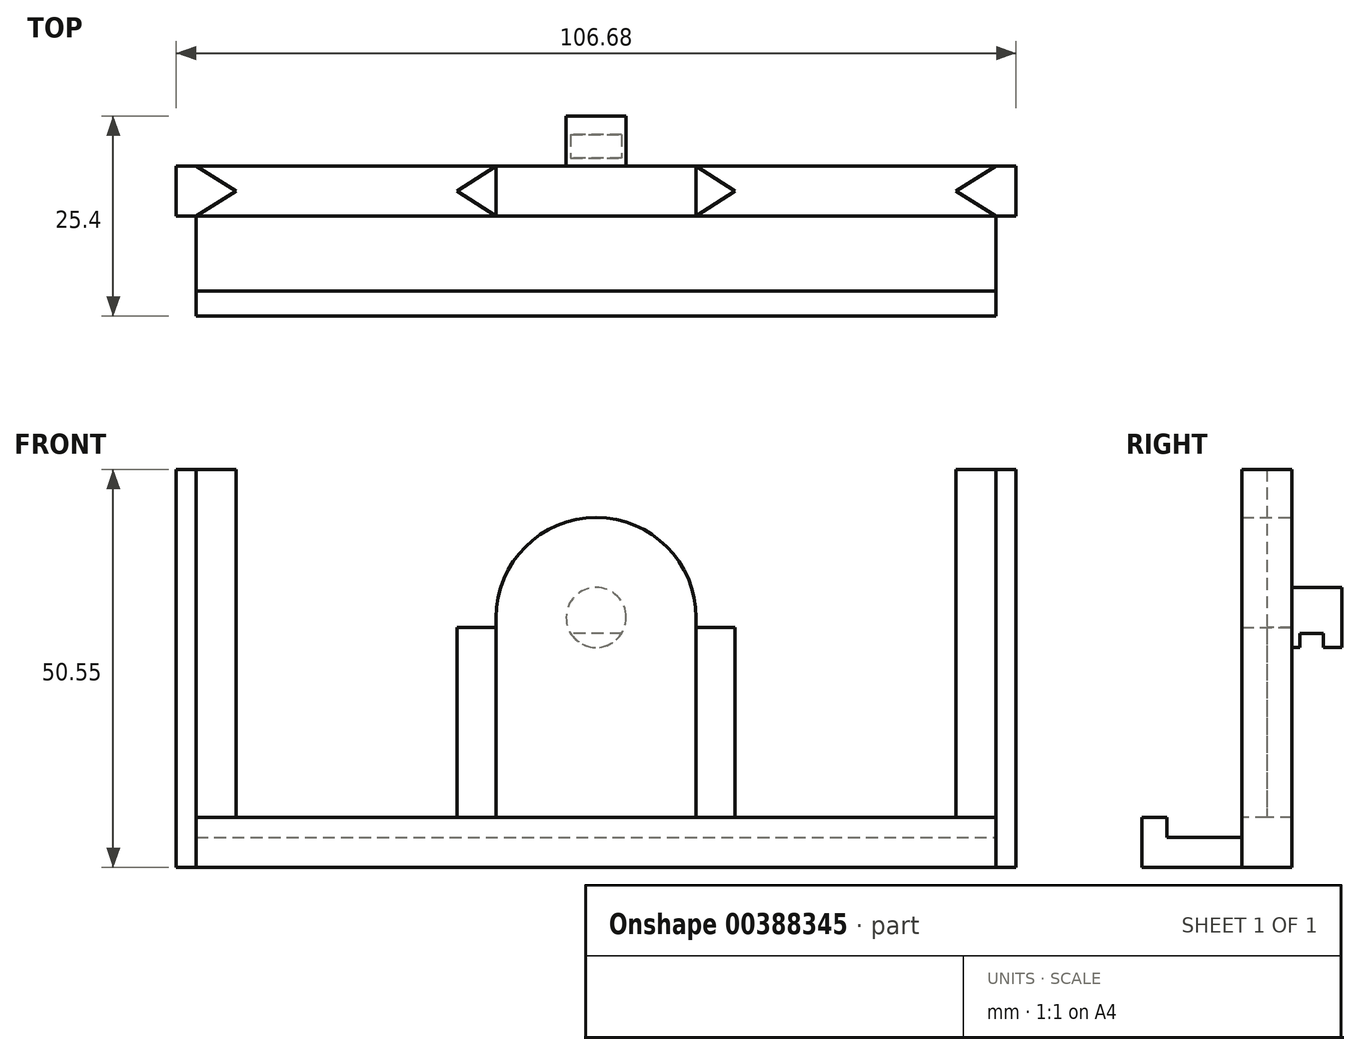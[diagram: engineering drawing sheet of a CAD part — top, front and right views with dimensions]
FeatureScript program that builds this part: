
annotation { "Feature Type Name" : "Feature", "Feature Type Description" : "" }
export const myFeature = defineFeature(function(context is Context, id is Id, definition is map)
    precondition{}
    {
        {
            var Q0;
            Q0=qCreatedBy(makeId("Front.planeOp"),FACE);
            var sketch = newSketch(context, id + "F0", { "sketchPlane" : qUnion([Q0])});
            skLineSegment(sketch, "E0.bottom", {"start": v(0, 0) * mm, "end": v(25.4, 0) * mm});
            skLineSegment(sketch, "E0.left", {"start": v(0, 0) * mm, "end": v(0, 25.4) * mm});
            skLineSegment(sketch, "E0.right", {"start": v(25.4, 0) * mm, "end": v(25.4, 25.4) * mm});
            skArc(sketch, "E1", {"start": v(25.4, 25.4) * mm, "mid": v(12.7, 38.1) * mm, "end": v(0, 25.4) * mm});
            skSolve(sketch);
        }
        {
            var Q0;
            Q0=qSketchRegion(id+"F0",true);
            extrude(context, id + "F1", {"entities" : qUnion([Q0]), "depth" : 6.35 * mm});
        }
        {
            var Q0;
            Q0=makeQuery(id+"F1.opExtrude","SWEPT_FACE",FACE,{"disambiguationData":[OSD([sQuery(id+"F0.wireOp",EDGE,"E0.bottom")])]});
            var sketch = newSketch(context, id + "F2", { "sketchPlane" : qUnion([Q0])});
            skPoint(sketch, "E2.endSnap0", {"position": v(25.4, 3.18) * mm});
            skLineSegment(sketch, "E3", {"start": v(0, 0) * mm, "end": v(-4.95, 3.18) * mm});
            skLineSegment(sketch, "E4", {"start": v(0, 6.35) * mm, "end": v(-4.95, 3.18) * mm});
            skLineSegment(sketch, "E5", {"start": v(25.4, 6.35) * mm, "end": v(30.35, 3.18) * mm});
            skLineSegment(sketch, "E6", {"start": v(30.35, 3.18) * mm, "end": v(30.35, 3.18) * mm});
            skLineSegment(sketch, "E7", {"start": v(25.4, 0) * mm, "end": v(30.35, 3.18) * mm});
            skPoint(sketch, "E8.start.orphan", {"position": v(0, 3.18) * mm});
            skPoint(sketch, "E2.start.orphan", {"position": v(25.4, 3.18) * mm});
            skLineSegment(sketch, "E9", {"start": v(0, 0) * mm, "end": v(0, 6.35) * mm});
            skLineSegment(sketch, "E10", {"start": v(25.4, 6.35) * mm, "end": v(25.4, 0) * mm});
            skSolve(sketch);
        }
        {
            var Q0;
            Q0=qSketchRegion(id+"F2",true);
            extrude(context, id + "F3", {"entities" : qUnion([Q0]), "operationType" : NewBodyOperationType.ADD, "oppositeDirection" : true, "depth" : 24.13 * mm});
        }
        {
            var Q0;
            Q0=makeQuery(id+"F3.boolean.opBoolean","MERGE",FACE,{"derivedFrom":[makeQuery(id+"F1.opExtrude","SWEPT_FACE",FACE,{"disambiguationData":[OSD([sQuery(id+"F0.wireOp",EDGE,"E0.bottom")])]}),makeQuery(id+"F3.opExtrude","CAP_FACE",FACE,{"disambiguationData":[OSD([sQuery(id+"F2.wireOp",EDGE,"E3"),sQuery(id+"F2.wireOp",EDGE,"E4"),sQuery(id+"F2.wireOp",EDGE,"E9")])],"isStart":true}),makeQuery(id+"F3.opExtrude","CAP_FACE",FACE,{"disambiguationData":[OSD([sQuery(id+"F2.wireOp",EDGE,"E5"),sQuery(id+"F2.wireOp",EDGE,"E7"),sQuery(id+"F2.wireOp",EDGE,"E10")])],"isStart":true})]});
            var sketch = newSketch(context, id + "F4", { "sketchPlane" : qUnion([Q0])});
            skLineSegment(sketch, "E11.bottom", {"start": v(63.5, 0) * mm, "end": v(-38.1, 0) * mm});
            skLineSegment(sketch, "E11.top", {"start": v(63.5, 6.35) * mm, "end": v(-38.1, 6.35) * mm});
            skLineSegment(sketch, "E11.left", {"start": v(63.5, 0) * mm, "end": v(63.5, 6.35) * mm});
            skLineSegment(sketch, "E11.right", {"start": v(-38.1, 0) * mm, "end": v(-38.1, 6.35) * mm});
            skSolve(sketch);
        }
        {
            var Q0;
            Q0=qSketchRegion(id+"F4",true);
            extrude(context, id + "F5", {"entities" : qUnion([Q0]), "operationType" : NewBodyOperationType.ADD, "depth" : 6.35 * mm});
        }
        {
            var Q0;
            Q0=makeQuery(id+"F5.boolean.opBoolean","MERGE",FACE,{"derivedFrom":[makeQuery(id+"F1.opExtrude","CAP_FACE",FACE,{"disambiguationData":[OSD([sQuery(id+"F0.wireOp",EDGE,"E0.bottom"),sQuery(id+"F0.wireOp",EDGE,"E0.left"),sQuery(id+"F0.wireOp",EDGE,"E0.right"),sQuery(id+"F0.wireOp",EDGE,"E1")])],"isStart":false}),makeQuery(id+"F5.opExtrude","SWEPT_FACE",FACE,{"disambiguationData":[OSD([sQuery(id+"F4.wireOp",EDGE,"E11.top")])]})]});
            var sketch = newSketch(context, id + "F6", { "sketchPlane" : qUnion([Q0])});
            skLineSegment(sketch, "E12", {"start": v(0, 0) * mm, "end": v(25.4, 0) * mm});
            skSolve(sketch);
        }
        {
            var Q0;
            Q0=qSketchRegion(id+"F6",true);
            var Q1;
            Q1=makeQuery(id+"F6.imprint","IMPRINT",FACE,{"disambiguationData":[TD([[makeQuery(id+"F6.imprint","IMPRINT",EDGE,{"derivedFrom":sQuery(id+"F6.wireOp",EDGE,"E12")}),-1.0]])]});
            extrude(context, id + "F7", {"entities" : qUnion([Q0, Q1]), "operationType" : NewBodyOperationType.ADD, "depth" : 12.7 * mm});
        }
        {
            var Q0;
            {var subQ0=sQuery(id+"F4.wireOp",EDGE,"E11.left");Q0=makeQuery(id+"F7.boolean.opBoolean","MERGE",FACE,{"derivedFrom":[makeQuery(id+"F5.opExtrude","SWEPT_FACE",FACE,{"disambiguationData":[OSD([subQ0])]}),makeQuery(id+"F7.opExtrude","SWEPT_FACE",FACE,{"disambiguationData":[OSD([sQuery(id+"F4.wireOp",EDGE,"E11.top"),subQ0])]})]});}
            var sketch = newSketch(context, id + "F8", { "sketchPlane" : qUnion([Q0])});
            skLineSegment(sketch, "E13.bottom", {"start": v(-15.87, 0) * mm, "end": v(-6.35, 0) * mm});
            skLineSegment(sketch, "E13.top", {"start": v(-15.87, -2.54) * mm, "end": v(-6.35, -2.54) * mm});
            skLineSegment(sketch, "E13.left", {"start": v(-15.87, 0) * mm, "end": v(-15.87, -2.54) * mm});
            skLineSegment(sketch, "E13.right", {"start": v(-6.35, 0) * mm, "end": v(-6.35, -2.54) * mm});
            skSolve(sketch);
        }
        {
            var Q0;
            Q0=qSketchRegion(id+"F8",true);
            extrude(context, id + "F9", {"entities" : qUnion([Q0]), "operationType" : NewBodyOperationType.REMOVE, "oppositeDirection" : true, "depth" : 114.28 * mm});
        }
        {
            var Q0;
            {var subQ0=sQuery(id+"F4.wireOp",EDGE,"E11.left");Q0=makeQuery(id+"F7.boolean.opBoolean","MERGE",FACE,{"derivedFrom":[makeQuery(id+"F5.opExtrude","SWEPT_FACE",FACE,{"disambiguationData":[OSD([subQ0])]}),makeQuery(id+"F7.opExtrude","SWEPT_FACE",FACE,{"disambiguationData":[OSD([sQuery(id+"F4.wireOp",EDGE,"E11.top"),subQ0])]})]});}
            var sketch = newSketch(context, id + "F10", { "sketchPlane" : qUnion([Q0])});
            skLineSegment(sketch, "E14", {"start": v(-6.35, 0) * mm, "end": v(-15.87, 0) * mm});
            skLineSegment(sketch, "E15", {"start": v(-6.35, 0) * mm, "end": v(-6.35, -6.35) * mm});
            skSolve(sketch);
        }
        {
            var Q0;
            {var subQ0=sQuery(id+"F10.wireOp",EDGE,"E14");Q0=makeQuery(id+"F10.imprint","IMPRINT",FACE,{"disambiguationData":[TD([[makeQuery(id+"F10.imprint","IMPRINT",EDGE,{"derivedFrom":subQ0}),1.0]])]});}
            extrude(context, id + "F11", {"entities" : qUnion([Q0]), "depth" : 12.7 * mm});
        }
        {
            var Q0;
            {var subQ0=sQuery(id+"F4.wireOp",EDGE,"E11.left");Q0=makeQuery(id+"F7.boolean.opBoolean","MERGE",FACE,{"derivedFrom":[makeQuery(id+"F5.opExtrude","SWEPT_FACE",FACE,{"disambiguationData":[OSD([subQ0])]}),makeQuery(id+"F7.opExtrude","SWEPT_FACE",FACE,{"disambiguationData":[OSD([sQuery(id+"F4.wireOp",EDGE,"E11.top"),subQ0])]})]});}
            var sketch = newSketch(context, id + "F12", { "sketchPlane" : qUnion([Q0])});
            skLineSegment(sketch, "E16", {"start": v(-6.35, -2.54) * mm, "end": v(-6.35, -6.35) * mm});
            skSolve(sketch);
        }
        {
            var Q0;
            Q0 = qSketchRegion(id + "F12", true);
            var Q1;
            {var subQ4=sQuery(id+"F12.wireOp",EDGE,"E16");Q1=makeQuery(id+"F12.imprint","IMPRINT",FACE,{"disambiguationData":[TD([[makeQuery(id+"F12.imprint","IMPRINT",EDGE,{"derivedFrom":subQ4}),-1.0]])]});}
            extrude(context, id + "F13", {"entities" : qUnion([Q0, Q1]), "depth" : 12.7 * mm});
        }
        {
            var Q0;
            {var subQ0=sQuery(id+"F4.wireOp",EDGE,"E11.right");Q0=makeQuery(id+"F7.boolean.opBoolean","MERGE",FACE,{"derivedFrom":[makeQuery(id+"F5.opExtrude","SWEPT_FACE",FACE,{"disambiguationData":[OSD([subQ0])]}),makeQuery(id+"F7.opExtrude","SWEPT_FACE",FACE,{"disambiguationData":[OSD([sQuery(id+"F4.wireOp",EDGE,"E11.top"),subQ0])]})]});}
            var sketch = newSketch(context, id + "F14", { "sketchPlane" : qUnion([Q0])});
            skLineSegment(sketch, "E17", {"start": v(6.35, 0) * mm, "end": v(15.87, 0) * mm});
            skSolve(sketch);
        }
        {
            var Q0;
            Q0=makeQuery(id+"F13.opExtrude","SWEPT_BODY",BODY,{"disambiguationData":[OSD([sQuery(id+"F4.wireOp",EDGE,"E11.top"),sQuery(id+"F4.wireOp",EDGE,"E11.left"),sQuery(id+"F8.wireOp",EDGE,"E13.top"),sQuery(id+"F8.wireOp",EDGE,"E13.left"),sQuery(id+"F12.wireOp",EDGE,"E16")])]});
            deleteBodies(context, id + "F15", {"entities" : qUnion([Q0])});
        }
        {
            var Q0;
            Q0=makeQuery(id+"F11.opExtrude","SWEPT_BODY",BODY,{"disambiguationData":[OSD([sQuery(id+"F8.wireOp",EDGE,"E13.top"),sQuery(id+"F8.wireOp",EDGE,"E13.left"),sQuery(id+"F10.wireOp",EDGE,"E14"),sQuery(id+"F10.wireOp",EDGE,"E15")])]});
            deleteBodies(context, id + "F16", {"entities" : qUnion([Q0])});
        }
        {
            var Q0;
            {var subQ0=makeQuery(id+"F3.opExtrude","SWEPT_FACE",FACE,{"disambiguationData":[OSD([sQuery(id+"F2.wireOp",EDGE,"E3")])]});var subQ8=sQuery(id+"F4.wireOp",EDGE,"E11.right");var subQ9=sQuery(id+"F4.wireOp",EDGE,"E11.top");var subQ10=sQuery(id+"F4.wireOp",EDGE,"E11.bottom");var subQ14=sQuery(id+"F4.wireOp",EDGE,"E11.left");var subQ15=makeQuery(id+"F5.opExtrude","CAP_FACE",FACE,{"disambiguationData":[OSD([subQ10,subQ9,subQ14,subQ8])],"isStart":true});Q0=makeQuery(id+"F9.boolean.opBoolean","SPLIT",FACE,{"disambiguationData":[TD([subQ0])],"derivedFrom":makeQuery(id+"F7.boolean.opBoolean","MERGE",FACE,{"derivedFrom":[makeQuery(id+"F5.boolean.opBoolean","SPLIT",FACE,{"disambiguationData":[TD([makeQuery(id+"F3.opExtrude","SWEPT_FACE",FACE,{"disambiguationData":[OSD([sQuery(id+"F2.wireOp",EDGE,"E5")])]})])],"derivedFrom":subQ15}),makeQuery(id+"F5.boolean.opBoolean","SPLIT",FACE,{"disambiguationData":[TD([subQ0])],"derivedFrom":subQ15}),makeQuery(id+"F7.opExtrude","SWEPT_FACE",FACE,{"disambiguationData":[OSD([subQ9,sQuery(id+"F6.wireOp",EDGE,"E12")])]})]})});}
            var sketch = newSketch(context, id + "F17", { "sketchPlane" : qUnion([Q0])});
            skLineSegment(sketch, "E18", {"start": v(-38.1, 0) * mm, "end": v(-38.1, -6.35) * mm});
            skLineSegment(sketch, "E19", {"start": v(-38.1, 0) * mm, "end": v(-33.02, -3.17) * mm});
            skLineSegment(sketch, "E20", {"start": v(-33.02, -3.17) * mm, "end": v(-33.02, -3.17) * mm});
            skLineSegment(sketch, "E21", {"start": v(-33.02, -3.17) * mm, "end": v(-38.1, -6.35) * mm});
            skPoint(sketch, "E22.start.orphan", {"position": v(-38.1, -3.17) * mm});
            skSolve(sketch);
        }
        {
            var Q0;
            {var subQ1=makeQuery(id+"F3.opExtrude","SWEPT_FACE",FACE,{"disambiguationData":[OSD([sQuery(id+"F2.wireOp",EDGE,"E5")])]});var subQ8=sQuery(id+"F4.wireOp",EDGE,"E11.bottom");var subQ10=sQuery(id+"F4.wireOp",EDGE,"E11.top");var subQ12=sQuery(id+"F4.wireOp",EDGE,"E11.left");var subQ14=sQuery(id+"F4.wireOp",EDGE,"E11.right");var subQ15=makeQuery(id+"F5.opExtrude","CAP_FACE",FACE,{"disambiguationData":[OSD([subQ8,subQ10,subQ12,subQ14])],"isStart":true});Q0=makeQuery(id+"F9.boolean.opBoolean","SPLIT",FACE,{"disambiguationData":[TD([subQ1])],"derivedFrom":makeQuery(id+"F7.boolean.opBoolean","MERGE",FACE,{"derivedFrom":[makeQuery(id+"F5.boolean.opBoolean","SPLIT",FACE,{"disambiguationData":[TD([subQ1])],"derivedFrom":subQ15}),makeQuery(id+"F5.boolean.opBoolean","SPLIT",FACE,{"disambiguationData":[TD([makeQuery(id+"F3.opExtrude","SWEPT_FACE",FACE,{"disambiguationData":[OSD([sQuery(id+"F2.wireOp",EDGE,"E3")])]})])],"derivedFrom":subQ15}),makeQuery(id+"F7.opExtrude","SWEPT_FACE",FACE,{"disambiguationData":[OSD([subQ10,sQuery(id+"F6.wireOp",EDGE,"E12")])]})]})});}
            var sketch = newSketch(context, id + "F18", { "sketchPlane" : qUnion([Q0])});
            skLineSegment(sketch, "E23", {"start": v(58.42, -3.18) * mm, "end": v(63.5, 0) * mm});
            skLineSegment(sketch, "E24", {"start": v(63.5, 0) * mm, "end": v(63.5, -6.35) * mm});
            skLineSegment(sketch, "E25", {"start": v(63.5, -6.35) * mm, "end": v(58.42, -3.17) * mm});
            skPoint(sketch, "E26.start.orphan", {"position": v(63.5, -3.18) * mm});
            skSolve(sketch);
        }
        {
            var Q0;
            Q0=makeQuery(id+"F18.imprint","IMPRINT",FACE,{"disambiguationData":[TD([[makeQuery(id+"F18.imprint","IMPRINT",EDGE,{"derivedFrom":sQuery(id+"F18.wireOp",EDGE,"E23")}),-1.0]])]});
            var Q1;
            Q1=makeQuery(id+"F17.imprint","IMPRINT",FACE,{"disambiguationData":[TD([[makeQuery(id+"F17.imprint","IMPRINT",EDGE,{"derivedFrom":sQuery(id+"F17.wireOp",EDGE,"E18")}),1.0]])]});
            extrude(context, id + "F19", {"entities" : qUnion([Q0, Q1]), "operationType" : NewBodyOperationType.ADD, "depth" : 44.2 * mm});
        }
        {
            var Q0;
            {var subQ0=sQuery(id+"F4.wireOp",EDGE,"E11.right");Q0=makeQuery(id+"F19.boolean.opBoolean","MERGE",FACE,{"derivedFrom":[makeQuery(id+"F7.boolean.opBoolean","MERGE",FACE,{"derivedFrom":[makeQuery(id+"F5.opExtrude","SWEPT_FACE",FACE,{"disambiguationData":[OSD([subQ0])]}),makeQuery(id+"F7.opExtrude","SWEPT_FACE",FACE,{"disambiguationData":[OSD([sQuery(id+"F4.wireOp",EDGE,"E11.top"),subQ0])]})]}),makeQuery(id+"F19.opExtrude","SWEPT_FACE",FACE,{"disambiguationData":[OSD([sQuery(id+"F17.wireOp",EDGE,"E18")])]})]});}
            var sketch = newSketch(context, id + "F20", { "sketchPlane" : qUnion([Q0])});
            skLineSegment(sketch, "E27", {"start": v(6.35, 0) * mm, "end": v(6.35, -6.35) * mm});
            skSolve(sketch);
        }
        {
            var Q0;
            Q0 = qSketchRegion(id + "F20", true);
            var Q1;
            {var subQ0=sQuery(id+"F17.wireOp",EDGE,"E18");Q1=makeQuery(id+"F20.imprint","IMPRINT",FACE,{"disambiguationData":[TD([[makeQuery(id+"F20.imprint","IMPRINT",EDGE,{"derivedFrom":makeQuery(id+"F19.opExtrude","CAP_EDGE",EDGE,{"disambiguationData":[OSD([subQ0])],"isStart":false})}),-1.0]])]});}
            extrude(context, id + "F21", {"entities" : qUnion([Q0, Q1]), "operationType" : NewBodyOperationType.ADD, "depth" : 2.54 * mm});
        }
        {
            var Q0;
            {var subQ0=sQuery(id+"F4.wireOp",EDGE,"E11.left");Q0=makeQuery(id+"F19.boolean.opBoolean","MERGE",FACE,{"derivedFrom":[makeQuery(id+"F7.boolean.opBoolean","MERGE",FACE,{"derivedFrom":[makeQuery(id+"F5.opExtrude","SWEPT_FACE",FACE,{"disambiguationData":[OSD([subQ0])]}),makeQuery(id+"F7.opExtrude","SWEPT_FACE",FACE,{"disambiguationData":[OSD([sQuery(id+"F4.wireOp",EDGE,"E11.top"),subQ0])]})]}),makeQuery(id+"F19.opExtrude","SWEPT_FACE",FACE,{"disambiguationData":[OSD([sQuery(id+"F18.wireOp",EDGE,"E24")])]})]});}
            var sketch = newSketch(context, id + "F22", { "sketchPlane" : qUnion([Q0])});
            skLineSegment(sketch, "E28", {"start": v(-6.35, -2.54) * mm, "end": v(-6.35, -6.35) * mm});
            skSolve(sketch);
        }
        {
            var Q0;
            Q0 = qSketchRegion(id + "F22", true);
            var Q1;
            {var subQ5=sQuery(id+"F22.wireOp",EDGE,"E28");Q1=makeQuery(id+"F22.imprint","IMPRINT",FACE,{"disambiguationData":[TD([[makeQuery(id+"F22.imprint","IMPRINT",EDGE,{"derivedFrom":subQ5}),1.0]])]});}
            extrude(context, id + "F23", {"entities" : qUnion([Q0, Q1]), "operationType" : NewBodyOperationType.ADD, "depth" : 2.54 * mm});
        }
        {
            var Q0;
            {var subQ0=sQuery(id+"F4.wireOp",EDGE,"E11.bottom");Q0=makeQuery(id+"F23.boolean.opBoolean","MERGE",FACE,{"derivedFrom":[makeQuery(id+"F21.boolean.opBoolean","MERGE",FACE,{"derivedFrom":[makeQuery(id+"F5.boolean.opBoolean","MERGE",FACE,{"derivedFrom":[makeQuery(id+"F1.opExtrude","CAP_FACE",FACE,{"disambiguationData":[OSD([sQuery(id+"F0.wireOp",EDGE,"E0.bottom"),sQuery(id+"F0.wireOp",EDGE,"E0.left"),sQuery(id+"F0.wireOp",EDGE,"E0.right"),sQuery(id+"F0.wireOp",EDGE,"E1")])],"isStart":true}),makeQuery(id+"F5.opExtrude","SWEPT_FACE",FACE,{"disambiguationData":[OSD([subQ0])]})]}),makeQuery(id+"F21.opExtrude","SWEPT_FACE",FACE,{"disambiguationData":[OSD([subQ0,sQuery(id+"F4.wireOp",EDGE,"E11.right"),sQuery(id+"F17.wireOp",EDGE,"E18"),sQuery(id+"F17.wireOp",EDGE,"E19")])]})]}),makeQuery(id+"F23.opExtrude","SWEPT_FACE",FACE,{"disambiguationData":[OSD([subQ0,sQuery(id+"F4.wireOp",EDGE,"E11.left"),sQuery(id+"F18.wireOp",EDGE,"E23"),sQuery(id+"F18.wireOp",EDGE,"E24")])]})]});}
            var sketch = newSketch(context, id + "F24", { "sketchPlane" : qUnion([Q0])});
            skCircle(sketch, "E29", {"center": v(-12.7, 25.4) * mm, "radius": 3.8 * mm});
            skSolve(sketch);
        }
        {
            var Q0;
            Q0 = qSketchRegion(id + "F24", true);
            extrude(context, id + "F25", {"entities" : qUnion([Q0]), "operationType" : NewBodyOperationType.ADD, "depth" : 6.35 * mm});
        }
        {
            var Q0;
            Q0=qCreatedBy(makeId("Right.planeOp"),FACE);
            var sketch = newSketch(context, id + "F26", { "sketchPlane" : qUnion([Q0])});
            skLineSegment(sketch, "E30.bottom", {"start": v(1.02, 20.33) * mm, "end": v(3.97, 20.33) * mm});
            skLineSegment(sketch, "E30.top", {"start": v(1.02, 23.4) * mm, "end": v(3.97, 23.4) * mm});
            skLineSegment(sketch, "E30.left", {"start": v(1.02, 20.33) * mm, "end": v(1.02, 23.4) * mm});
            skLineSegment(sketch, "E30.right", {"start": v(3.97, 20.33) * mm, "end": v(3.97, 23.4) * mm});
            skSolve(sketch);
        }
        {
            var Q0;
            Q0=makeQuery(id+"F26.imprint","IMPRINT",FACE,{"disambiguationData":[TD([[makeQuery(id+"F26.imprint","IMPRINT",EDGE,{"derivedFrom":sQuery(id+"F26.wireOp",EDGE,"E30.bottom")}),1.0]])]});
            extrude(context, id + "F27", {"entities" : qUnion([Q0]), "operationType" : NewBodyOperationType.REMOVE, "depth" : 20.52 * mm});
        }
    });
